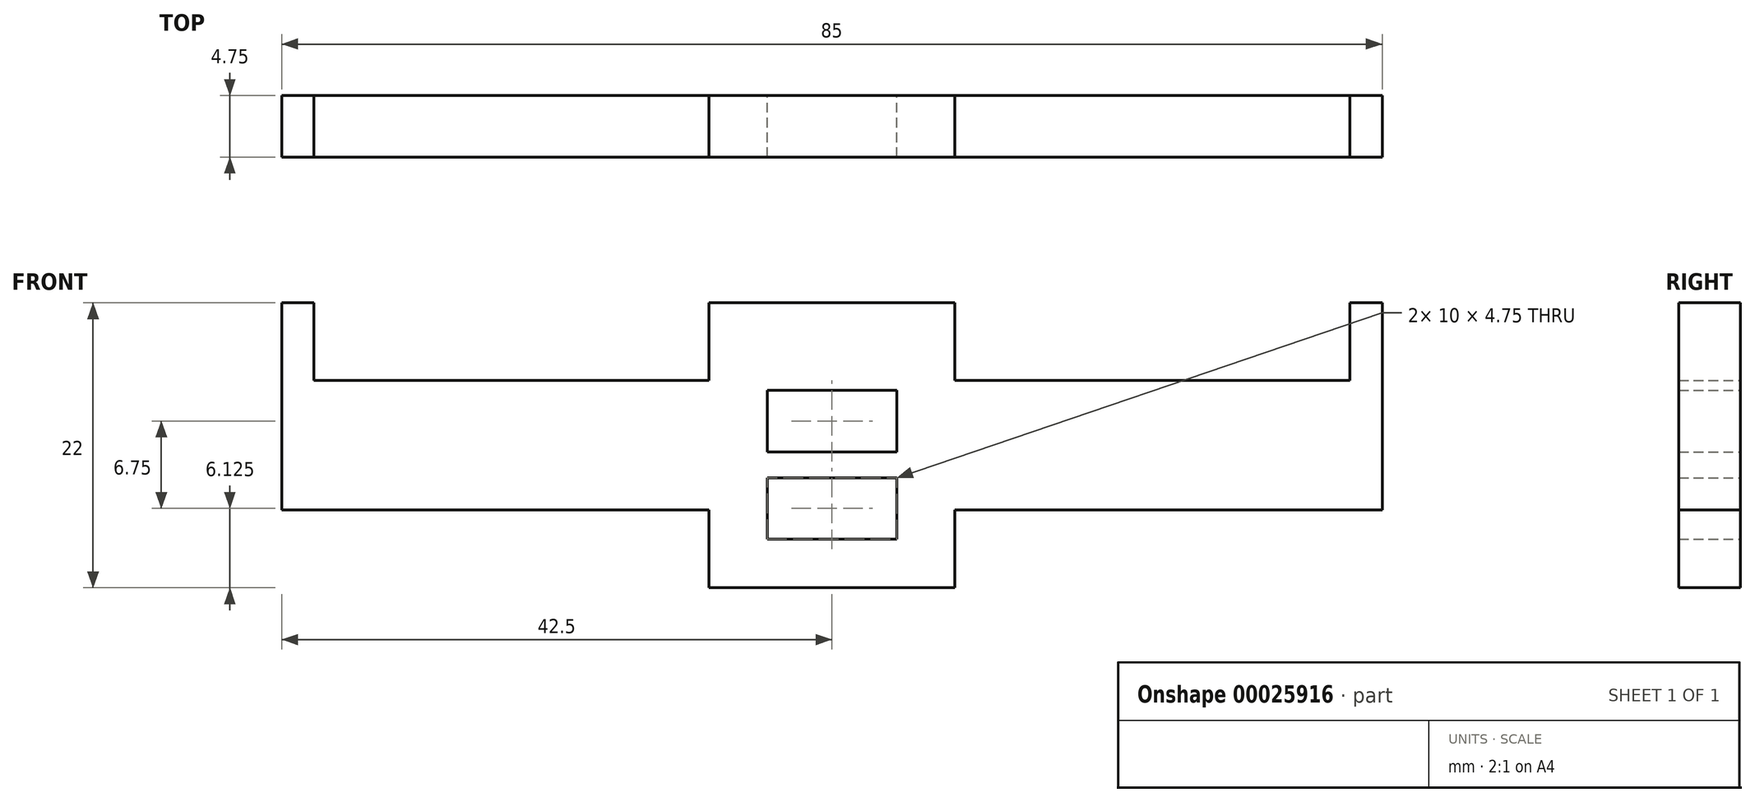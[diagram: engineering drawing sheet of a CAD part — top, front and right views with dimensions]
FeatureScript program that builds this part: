
annotation { "Feature Type Name" : "Feature", "Feature Type Description" : "" }
export const myFeature = defineFeature(function(context is Context, id is Id, definition is map)
    precondition{}
    {
        {
            var Q0;
            Q0=qCreatedBy(makeId("Front.planeOp"),FACE);
            var sketch = newSketch(context, id + "F0", { "sketchPlane" : qUnion([Q0])});
            skLineSegment(sketch, "E0", {"start": v(0, -6) * mm, "end": v(9.5, -6) * mm});
            skLineSegment(sketch, "E1", {"start": v(9.5, -6) * mm, "end": v(9.5, 0) * mm});
            skLineSegment(sketch, "E2", {"start": v(42.5, 16) * mm, "end": v(40, 16) * mm});
            skLineSegment(sketch, "E3", {"start": v(40, 16) * mm, "end": v(40, 10) * mm});
            skLineSegment(sketch, "E4", {"start": v(40, 10) * mm, "end": v(9.5, 10) * mm});
            skLineSegment(sketch, "E5", {"start": v(9.5, 10) * mm, "end": v(9.5, 16) * mm});
            skLineSegment(sketch, "E6", {"start": v(9.5, 16) * mm, "end": v(0, 16) * mm});
            skLineSegment(sketch, "E7", {"start": v(0, 16) * mm, "end": v(0, 9.25) * mm});
            skLineSegment(sketch, "E8.bottom", {"start": v(0, 9.25) * mm, "end": v(5, 9.25) * mm});
            skLineSegment(sketch, "E8.top", {"start": v(0, 4.5) * mm, "end": v(5, 4.5) * mm});
            skLineSegment(sketch, "E8.right", {"start": v(5, 9.25) * mm, "end": v(5, 4.5) * mm});
            skLineSegment(sketch, "E9.bottom", {"start": v(0, 2.5) * mm, "end": v(5, 2.5) * mm});
            skLineSegment(sketch, "E9.top", {"start": v(0, -2.25) * mm, "end": v(5, -2.25) * mm});
            skLineSegment(sketch, "E9.right", {"start": v(5, 2.5) * mm, "end": v(5, -2.25) * mm});
            skLineSegment(sketch, "E10.trimOffspring", {"start": v(0, -2.25) * mm, "end": v(0, -6) * mm});
            skLineSegment(sketch, "E11.trimOffspring", {"start": v(0, 4.5) * mm, "end": v(0, 2.5) * mm});
            skLineSegment(sketch, "E12", {"start": v(42.5, 16) * mm, "end": v(42.5, 0) * mm});
            skLineSegment(sketch, "E13", {"start": v(9.5, 0) * mm, "end": v(42.5, 0) * mm});
            skSolve(sketch);
        }
        {
            var Q0;
            Q0=makeQuery(id+"F0.imprint","IMPRINT",FACE,{"disambiguationData":[TD([[makeQuery(id+"F0.imprint","IMPRINT",EDGE,{"derivedFrom":sQuery(id+"F0.wireOp",EDGE,"E0")}),1.0]])]});
            extrude(context, id + "F1", {"entities" : qUnion([Q0]), "depth" : 4.75 * mm});
        }
        {
            var Q0;
            Q0=makeQuery(id+"F1.opExtrude","SWEPT_BODY",BODY,{"disambiguationData":[OSD([sQuery(id+"F0.wireOp",EDGE,"E0"),sQuery(id+"F0.wireOp",EDGE,"E1"),sQuery(id+"F0.wireOp",EDGE,"98c0ea5d-fe56-44f3-9d33-ca233d41d53c"),sQuery(id+"F0.wireOp",EDGE,"444717f7-6fb8-4ccd-a88c-3b946ee9808f"),sQuery(id+"F0.wireOp",EDGE,"b3c24bc2-6bbe-4ad2-9781-57c514dc2c93"),sQuery(id+"F0.wireOp",EDGE,"5df89fef-cbd9-4053-a4b6-b904276b5e75"),sQuery(id+"F0.wireOp",EDGE,"d1567a0b-1f64-4543-b28b-fb29c987b7e9"),sQuery(id+"F0.wireOp",EDGE,"18562130-1496-44c8-9b62-2a2a88a68ef8"),sQuery(id+"F0.wireOp",EDGE,"E2"),sQuery(id+"F0.wireOp",EDGE,"E3"),sQuery(id+"F0.wireOp",EDGE,"E4"),sQuery(id+"F0.wireOp",EDGE,"E5"),sQuery(id+"F0.wireOp",EDGE,"E6"),sQuery(id+"F0.wireOp",EDGE,"E7")])]});
            var Q1;
            Q1=qCreatedBy(makeId("Right.planeOp"),FACE);
            mirror(context, id + "F2", {"operationType" : NewBodyOperationType.ADD, "entities" : qUnion([Q0]), "mirrorPlane" : qUnion([Q1])});
        }
    });
